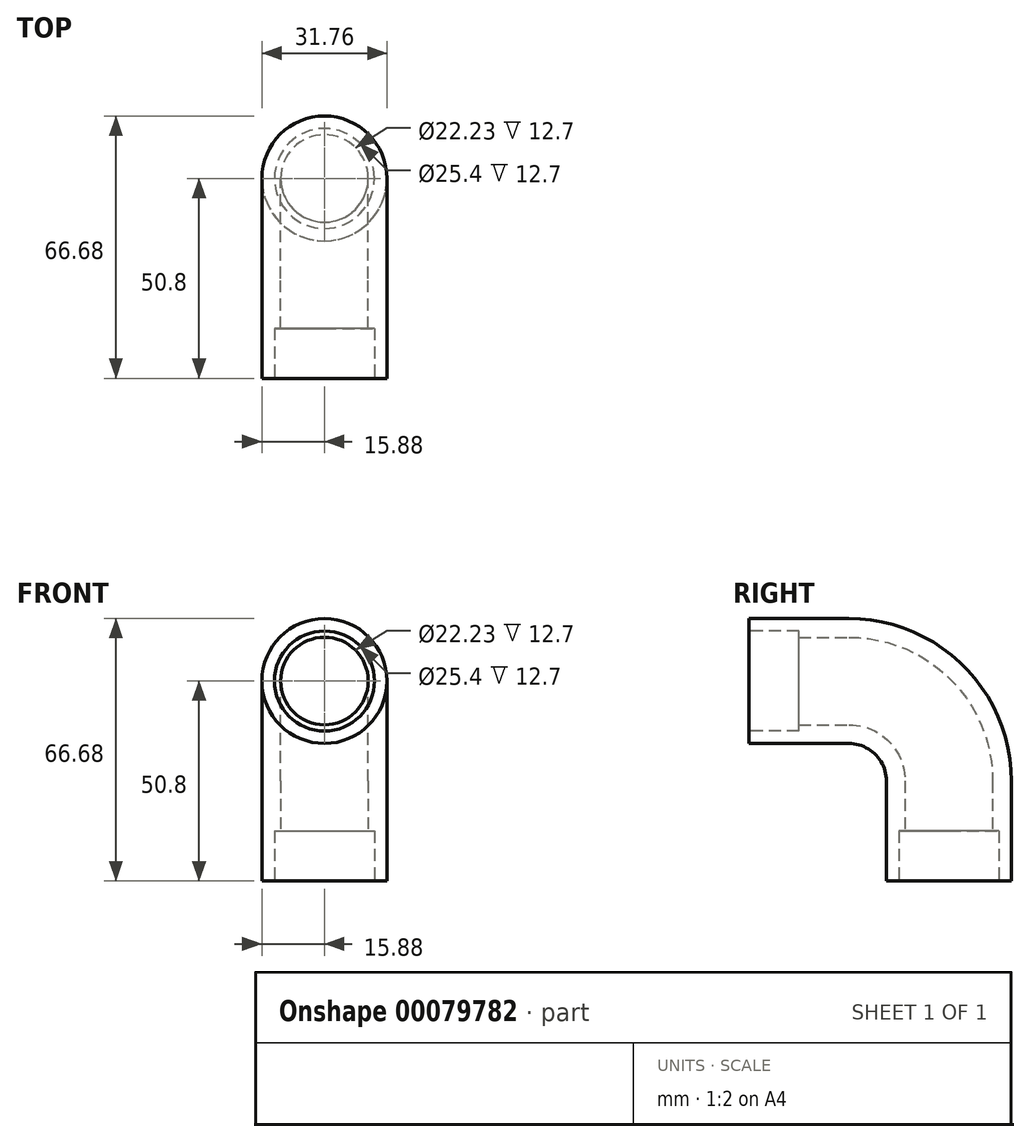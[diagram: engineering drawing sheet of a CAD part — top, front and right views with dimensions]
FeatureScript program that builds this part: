
annotation { "Feature Type Name" : "Feature", "Feature Type Description" : "" }
export const myFeature = defineFeature(function(context is Context, id is Id, definition is map)
    precondition{}
    {
        {
            var Q0;
            Q0=qCreatedBy(makeId("Front.planeOp"),FACE);
            var sketch = newSketch(context, id + "F0", { "sketchPlane" : qUnion([Q0])});
            skCircle(sketch, "E0", {"center": v(0, 0) * mm, "radius": 15.88 * mm});
            skCircle(sketch, "E1", {"center": v(0, 0) * mm, "radius": 11.11 * mm});
            skSolve(sketch);
        }
        {
            var Q0;
            Q0=qCreatedBy(makeId("Right.planeOp"),FACE);
            var sketch = newSketch(context, id + "F1", { "sketchPlane" : qUnion([Q0])});
            skLineSegment(sketch, "E2", {"start": v(0, 0) * mm, "end": v(25.4, 0) * mm});
            skLineSegment(sketch, "E3", {"start": v(50.8, -25.4) * mm, "end": v(50.8, -50.8) * mm});
            skPoint(sketch, "E4.visualSharp", {"position": v(50.8, 0) * mm});
            skArc(sketch, "E4.filletArc", {"start": v(50.8, -25.4) * mm, "mid": v(43.36, -7.44) * mm, "end": v(25.4, 0) * mm});
            skSolve(sketch);
        }
        {
            var Q0;
            Q0=makeQuery(id+"F0.imprint","IMPRINT",FACE,{"disambiguationData":[TD([[makeQuery(id+"F0.imprint","IMPRINT",EDGE,{"derivedFrom":sQuery(id+"F0.wireOp",EDGE,"E0")}),1.0]])]});
            var Q1;
            Q1=sQuery(id+"F1.wireOp",EDGE,"E2");
            var Q2;
            Q2=sQuery(id+"F1.wireOp",EDGE,"E4.filletArc");
            var Q3;
            Q3=sQuery(id+"F1.wireOp",EDGE,"E3");
            sweep(context, id + "F2", {"profiles" : qUnion([Q0]), "path" : qUnion([Q1, Q2, Q3])});
        }
        {
            var Q0;
            Q0=makeQuery(id+"F2.opSweep","CAP_FACE",FACE,{"disambiguationData":[OSD([sQuery(id+"F0.wireOp",EDGE,"E0"),sQuery(id+"F0.wireOp",EDGE,"E1"),sQuery(id+"F1.wireOp",VERTEX,"E2.start")])],"isStart":true});
            var sketch = newSketch(context, id + "F3", { "sketchPlane" : qUnion([Q0])});
            skCircle(sketch, "E5", {"center": v(0, 0) * mm, "radius": 12.7 * mm});
            skSolve(sketch);
        }
        {
            var Q0;
            Q0=makeQuery(id+"F3.imprint","IMPRINT",FACE,{"disambiguationData":[TD([[makeQuery(id+"F3.imprint","IMPRINT",EDGE,{"derivedFrom":sQuery(id+"F3.wireOp",EDGE,"E5")}),1.0]])]});
            extrude(context, id + "F4", {"entities" : qUnion([Q0]), "operationType" : NewBodyOperationType.REMOVE, "oppositeDirection" : true, "depth" : 12.7 * mm});
        }
        {
            var Q0;
            Q0=makeQuery(id+"F2.opSweep","CAP_FACE",FACE,{"disambiguationData":[OSD([sQuery(id+"F0.wireOp",EDGE,"E0"),sQuery(id+"F0.wireOp",EDGE,"E1"),sQuery(id+"F1.wireOp",VERTEX,"E3.end")])],"isStart":false});
            var sketch = newSketch(context, id + "F5", { "sketchPlane" : qUnion([Q0])});
            skCircle(sketch, "E6", {"center": v(0, -50.8) * mm, "radius": 12.7 * mm});
            skSolve(sketch);
        }
        {
            var Q0;
            Q0 = qSketchRegion(id + "F5", true);
            extrude(context, id + "F6", {"entities" : qUnion([Q0]), "operationType" : NewBodyOperationType.REMOVE, "oppositeDirection" : true, "depth" : 12.7 * mm});
        }
    });
